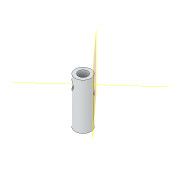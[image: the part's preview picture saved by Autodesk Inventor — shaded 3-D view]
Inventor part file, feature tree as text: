
AUTODESK INVENTOR PART (.ipt)
format: ipt  version: 2017 (Build 210142000, 142)  size: 149,504 bytes
history: native  units: in
note: dims shown in document units (in); Inventor stores cm internally (conversion verified against a paired STEP export)
features: other x3, extrude x2, sketch x2, plane x1, projected_geometry x1
ambient origin geometry x8: Origin, YZ Plane, XZ Plane, XY Plane, X Axis, Y Axis, Z Axis, Center Point
bodies: Solid1 (feature_tree)
feature tree (9):
  plane  "Work Plane1"
  extrude  "Extrusion1"  Depth=0.0394in TaperAngle=0.0deg
  extrude  "Extrusion2"  [1 undecoded]
  other  "Work Axis1"
  other  "Work Point1"
  sketch  "Sketch1"  dims[d0=0.0625in d1=0.0394in d2=0.0in]
  sketch  "Sketch2"  dims[d3=0.3937in d4=0.0in]
  projected_geometry  "Projected Loop1"
  other  "1_64 (0.01563) Diameter Hole3"
note: 1 required parameter value undecoded (feature->parameter linkage not recoverable at this tier; creation-order binding heuristic only, values carry confidence <= 0.55)
